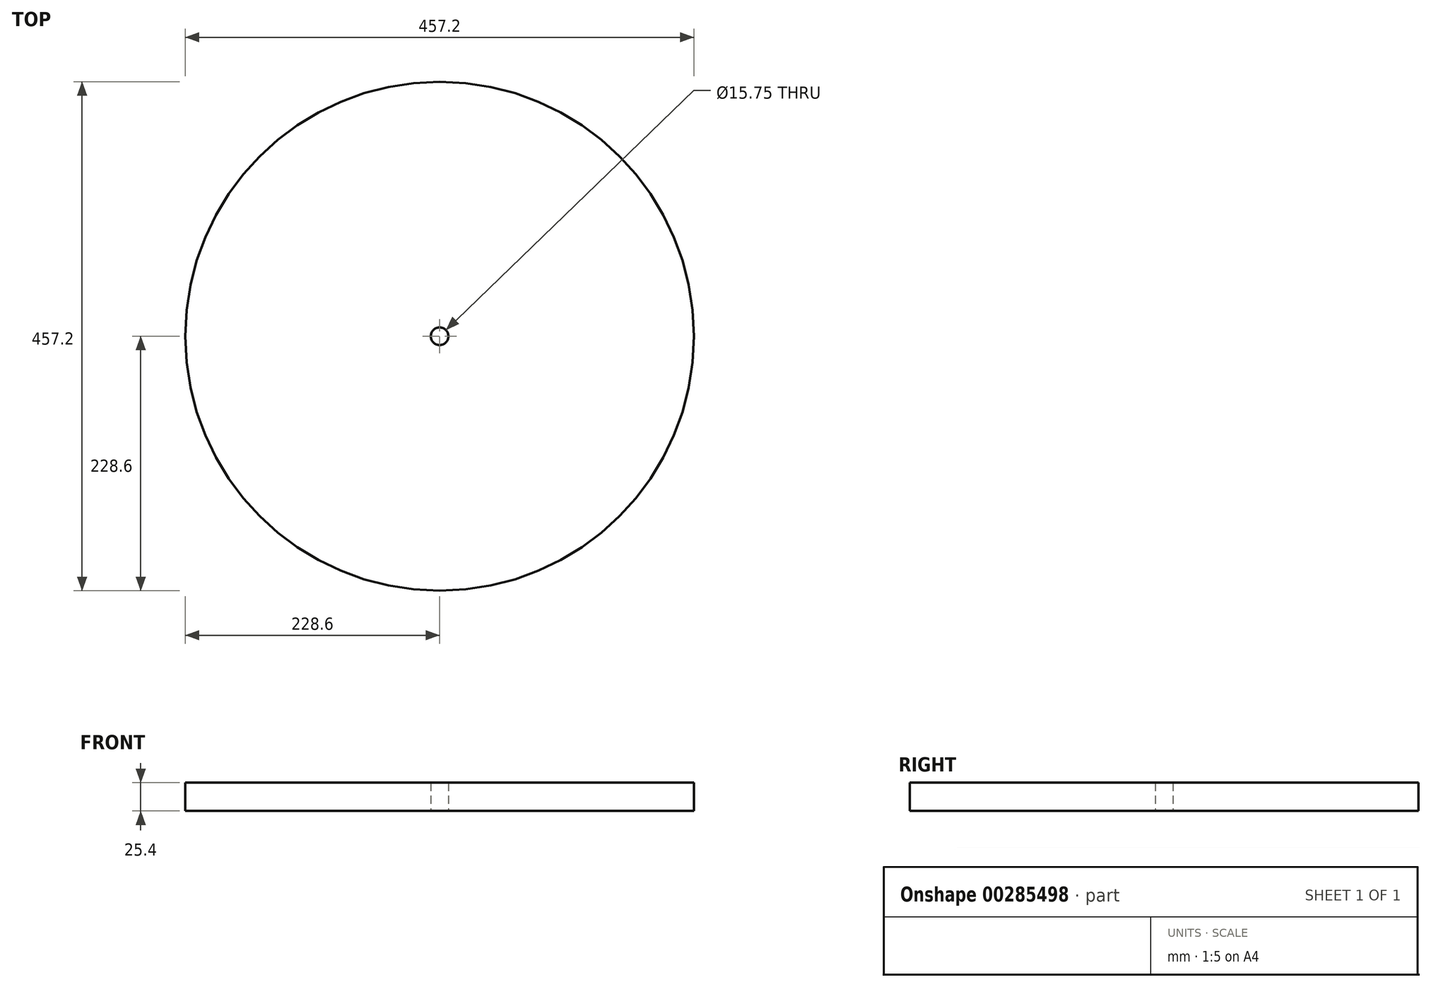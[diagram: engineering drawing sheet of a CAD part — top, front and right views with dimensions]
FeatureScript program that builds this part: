
annotation { "Feature Type Name" : "Feature", "Feature Type Description" : "" }
export const myFeature = defineFeature(function(context is Context, id is Id, definition is map)
    precondition{}
    {
        {
            var Q0;
            Q0=qCreatedBy(makeId("Top.planeOp"),FACE);
            var sketch = newSketch(context, id + "F0", { "sketchPlane" : qUnion([Q0])});
            skCircle(sketch, "E0", {"center": v(0, 0) * mm, "radius": 228.6 * mm});
            skCircle(sketch, "E1", {"center": v(0, 0) * mm, "radius": 7.87 * mm});
            skSolve(sketch);
        }
        {
            var Q0;
            Q0=makeQuery(id+"F0.imprint","IMPRINT",FACE,{"disambiguationData":[TD([[makeQuery(id+"F0.imprint","IMPRINT",EDGE,{"derivedFrom":sQuery(id+"F0.wireOp",EDGE,"E0")}),1.0]])]});
            extrude(context, id + "F1", {"entities" : qUnion([Q0]), "depth" : 25.4 * mm});
        }
    });
